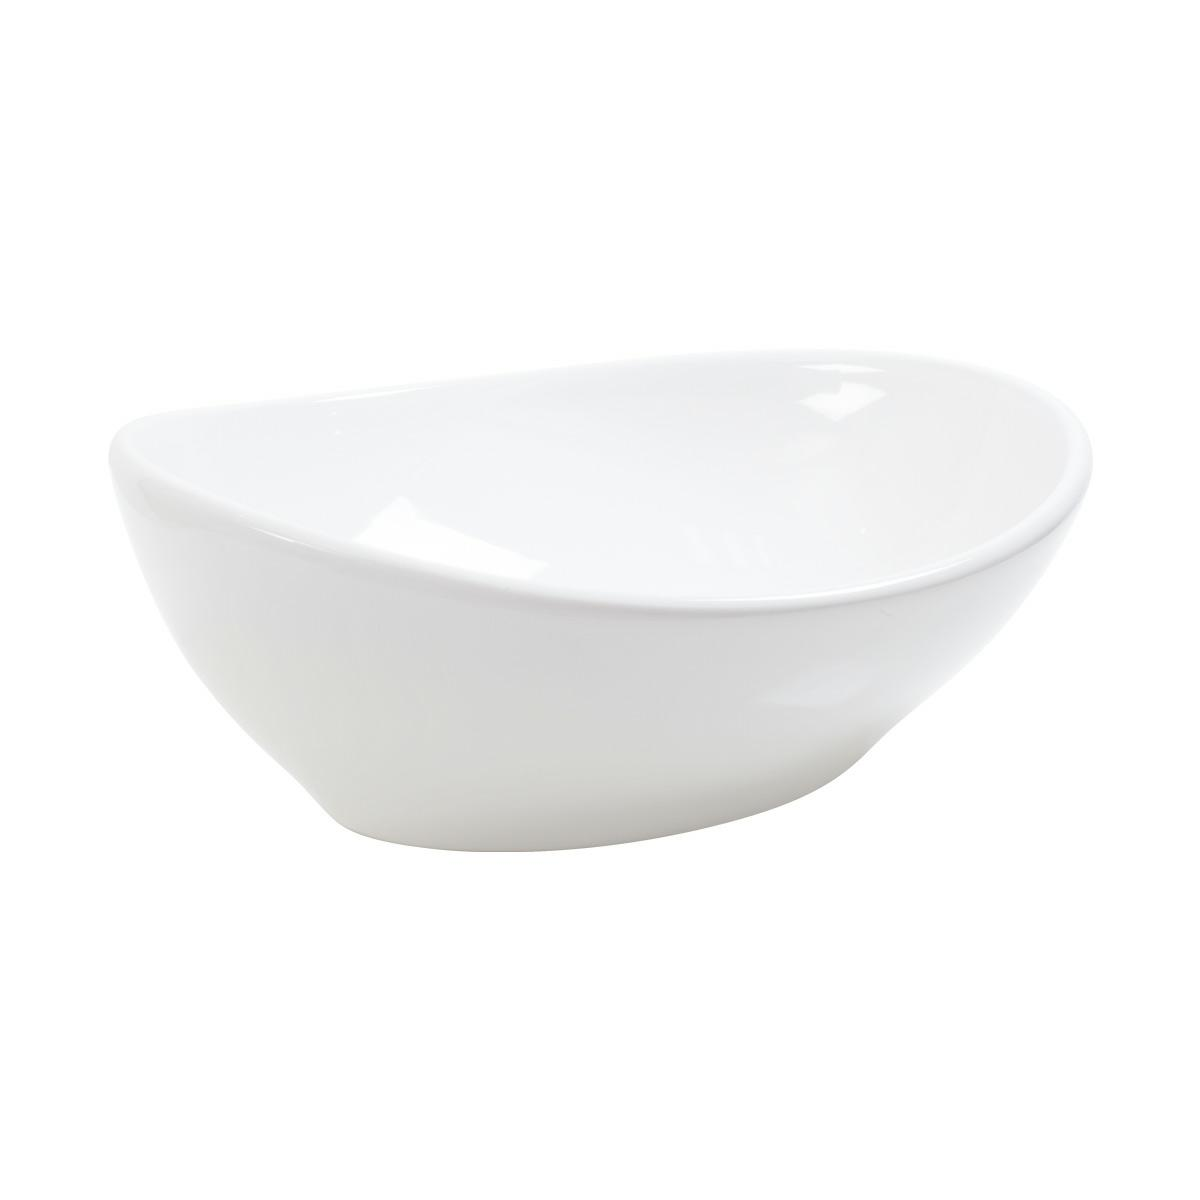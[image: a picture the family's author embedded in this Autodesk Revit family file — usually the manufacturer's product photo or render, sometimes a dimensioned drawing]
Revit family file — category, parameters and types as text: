
# Revit family: CCMX-CORONA_RAVENNA
name_source: partatom
category: Plumbing Fixtures
units: mm (PartAtom-declared; Revit-internal decimal feet)

## family parameters
Always vertical = Yes
Cut with Voids When Loaded = No
OmniClass Number = 23.45.00.00
OmniClass Title = Sanitary, Laundry, and Cleaning Equipment
Part Type = Normal
Room Calculation Point = No
Round Connector Dimension = Use Diameter
Shared = No
Work Plane-Based = No

## types (1)
- CCMX-CORONA_RAVENNA
    Assembly Code = D2010.60
    Description = Lavamanos Vessel de práctico tamaño y con diseño innovador y contemporáneo. Se recomienda instalar con griferías a la pared o de mesón altas.
    Dimensiones = https://coronamexico.com
    Ficha Tecnica = https://coronamexico.com
    Garantia de Producto = 20 años en porcelana sanitaria
    Keynote = 224116
    Manufacturer = CORONA
    Model = Ravenna
    Type Image = RAVENNA_.jpg
    URL = https://coronamexico.com

## geometry (parser evidence)
native form markers: Sweep x3
no freeform markers — native parametric forms only
